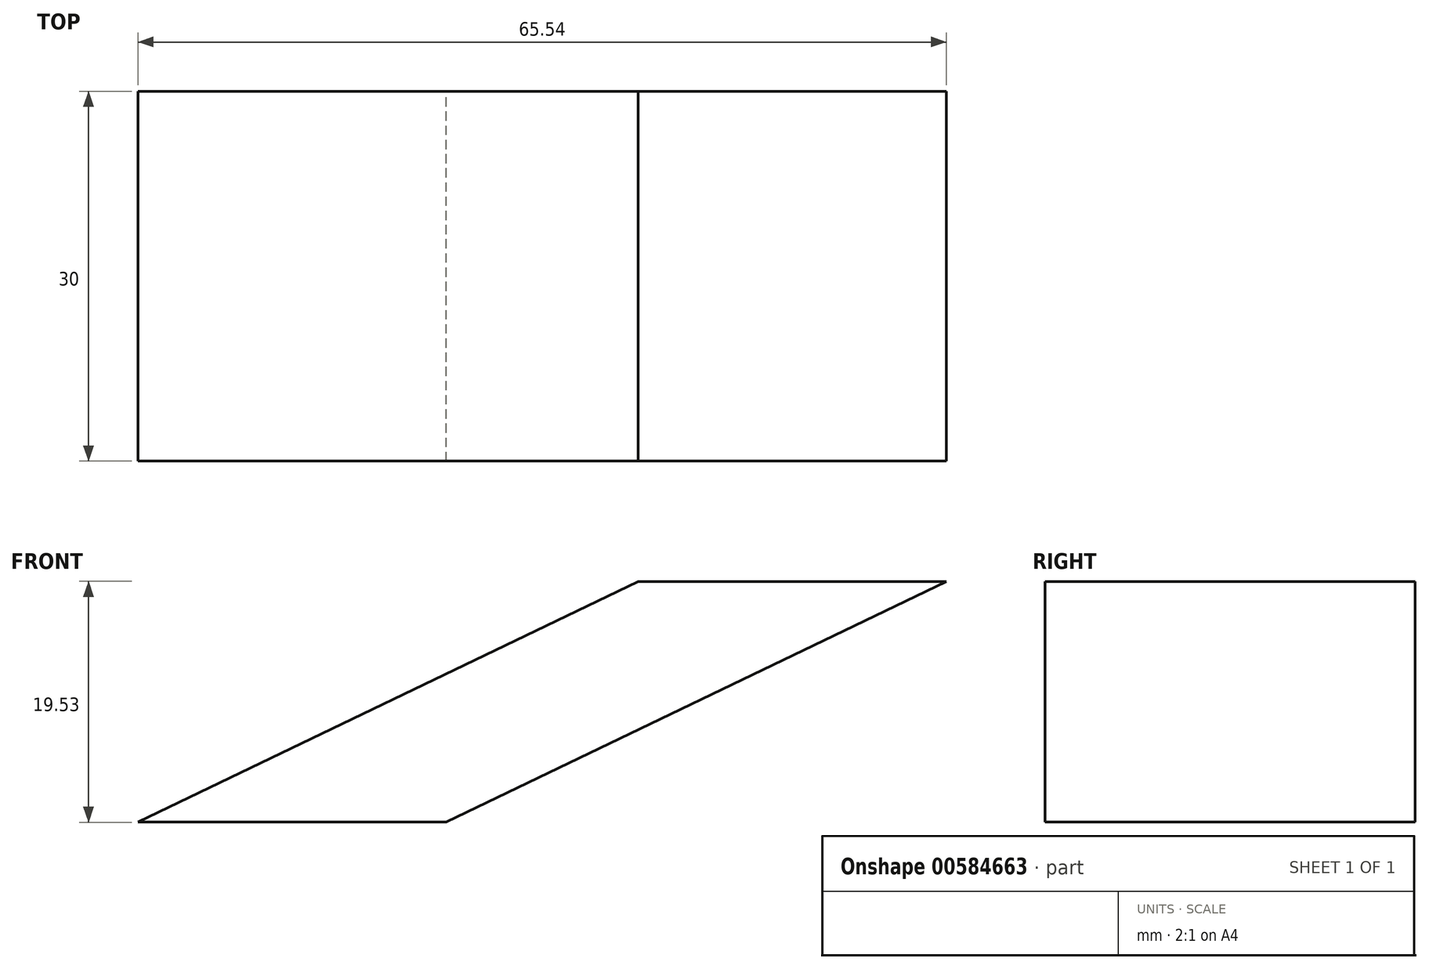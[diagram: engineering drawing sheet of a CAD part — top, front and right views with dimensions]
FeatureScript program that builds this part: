
annotation { "Feature Type Name" : "Feature", "Feature Type Description" : "" }
export const myFeature = defineFeature(function(context is Context, id is Id, definition is map)
    precondition{}
    {
        {
            var Q0;
            Q0=qCreatedBy(makeId("Front.planeOp"),FACE);
            var sketch = newSketch(context, id + "F0", { "sketchPlane" : qUnion([Q0])});
            skLineSegment(sketch, "E0", {"start": v(-24.08, -12.14) * mm, "end": v(0.92, -12.14) * mm});
            skLineSegment(sketch, "E1", {"start": v(-24.08, -12.14) * mm, "end": v(16.46, 7.39) * mm});
            skLineSegment(sketch, "E2", {"start": v(0.92, -12.14) * mm, "end": v(41.46, 7.39) * mm});
            skLineSegment(sketch, "E3", {"start": v(16.46, 7.39) * mm, "end": v(41.46, 7.39) * mm});
            skSolve(sketch);
        }
        {
            var Q0;
            Q0=makeQuery(id+"F0.imprint","IMPRINT",FACE,{"disambiguationData":[TD([[makeQuery(id+"F0.imprint","IMPRINT",EDGE,{"derivedFrom":sQuery(id+"F0.wireOp",EDGE,"E0")}),1.0]])]});
            extrude(context, id + "F1", {"entities" : qUnion([Q0]), "depth" : 30 * mm, "offsetDistance" : 25 * mm});
        }
    });
